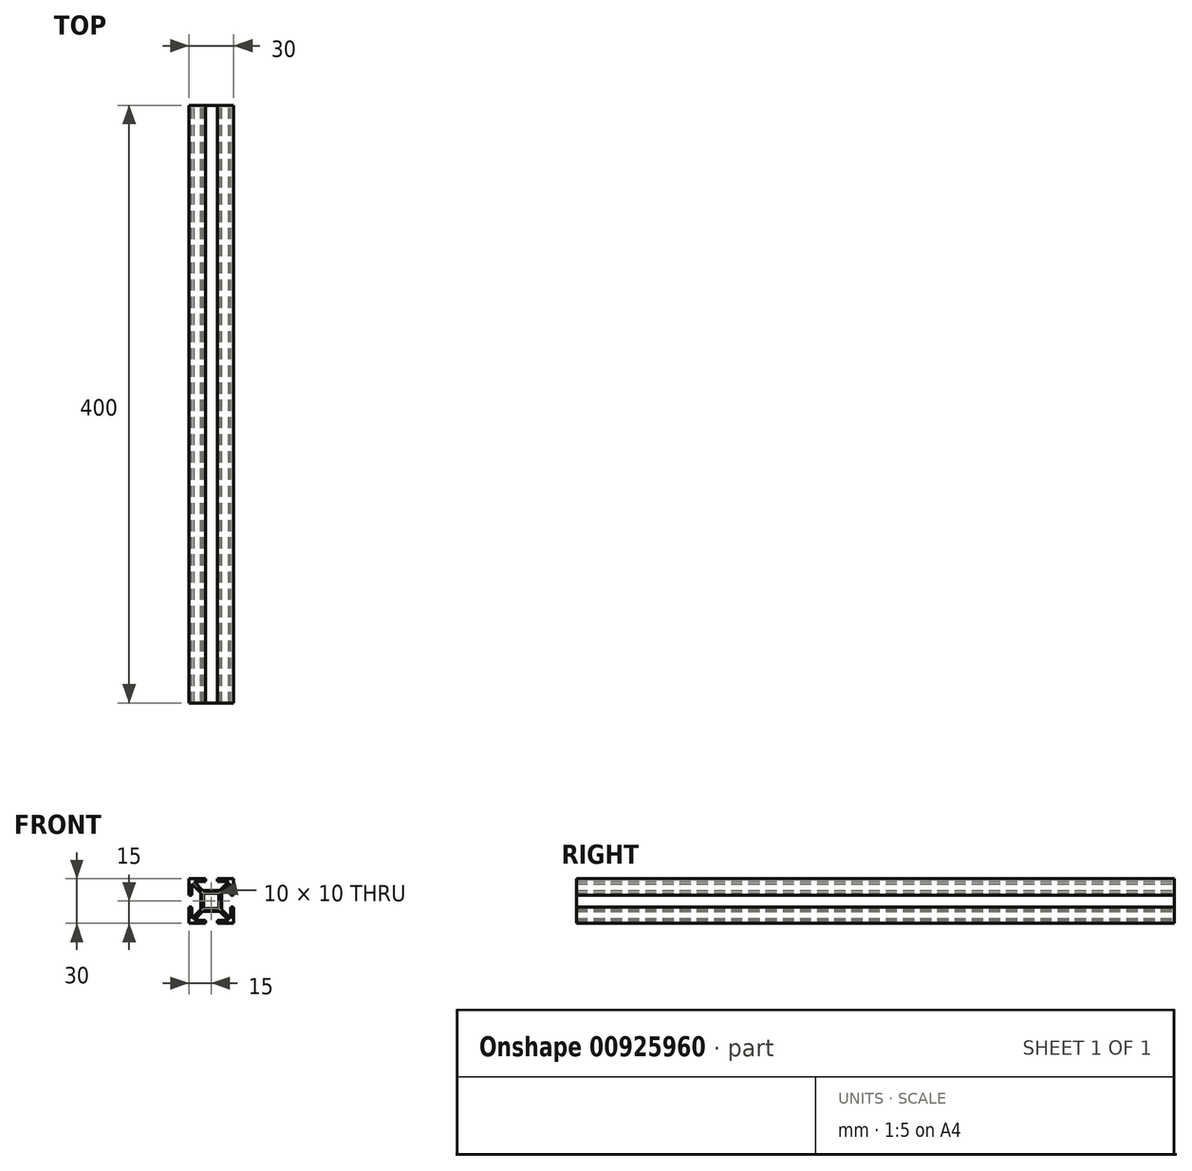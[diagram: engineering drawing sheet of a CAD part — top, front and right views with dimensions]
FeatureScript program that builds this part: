
annotation { "Feature Type Name" : "Feature", "Feature Type Description" : "" }
export const myFeature = defineFeature(function(context is Context, id is Id, definition is map)
    precondition{}
    {
        {
            var Q0;
            Q0=qCreatedBy(makeId("Front.planeOp"),FACE);
            var sketch = newSketch(context, id + "F0", { "sketchPlane" : qUnion([Q0])});
            skLineSegment(sketch, "E0.bottom", {"start": v(5, 5) * mm, "end": v(-5, 5) * mm});
            skLineSegment(sketch, "E0.top", {"start": v(5, -5) * mm, "end": v(-5, -5) * mm});
            skLineSegment(sketch, "E0.left", {"start": v(5, 5) * mm, "end": v(5, -5) * mm});
            skLineSegment(sketch, "E0.right", {"start": v(-5, 5) * mm, "end": v(-5, -5) * mm});
            skPoint(sketch, "E0.middle", {"position": v(0, 0) * mm});
            skLineSegment(sketch, "E1.0", {"start": v(7, -7) * mm, "end": v(-7, -7) * mm});
            skLineSegment(sketch, "E1.1", {"start": v(7, 7) * mm, "end": v(7, -7) * mm});
            skLineSegment(sketch, "E1.2", {"start": v(7, 7) * mm, "end": v(-7, 7) * mm});
            skLineSegment(sketch, "E1.3", {"start": v(-7, 7) * mm, "end": v(-7, -7) * mm});
            skLineSegment(sketch, "E2", {"start": v(-7, 7) * mm, "end": v(-13.08, 13.08) * mm, "construction": true});
            skLineSegment(sketch, "E3", {"start": v(-7, 5.59) * mm, "end": v(-13, 11.59) * mm});
            skLineSegment(sketch, "E4", {"start": v(-5.59, 7) * mm, "end": v(-11.59, 13) * mm});
            skLineSegment(sketch, "E5", {"start": v(-11.59, 13) * mm, "end": v(-4, 13) * mm});
            skLineSegment(sketch, "E6", {"start": v(-4, 13) * mm, "end": v(-4, 15) * mm});
            skLineSegment(sketch, "E7", {"start": v(-4, 15) * mm, "end": v(-15, 15) * mm});
            skLineSegment(sketch, "E8", {"start": v(-15, 15) * mm, "end": v(-15, 4) * mm});
            skLineSegment(sketch, "E9", {"start": v(-15, 4) * mm, "end": v(-13, 4) * mm});
            skLineSegment(sketch, "E10", {"start": v(-13, 4) * mm, "end": v(-13, 11.59) * mm});
            skLineSegment(sketch, "E11.1.0", {"start": v(-7, -7) * mm, "end": v(-13.08, -13.08) * mm, "construction": true});
            skLineSegment(sketch, "E11.1.1", {"start": v(-15, -4) * mm, "end": v(-15, -15) * mm});
            skLineSegment(sketch, "E11.1.2", {"start": v(-4, -13) * mm, "end": v(-11.59, -13) * mm});
            skLineSegment(sketch, "E11.1.3", {"start": v(-4, -15) * mm, "end": v(-4, -13) * mm});
            skLineSegment(sketch, "E11.1.4", {"start": v(-5.59, -7) * mm, "end": v(-11.59, -13) * mm});
            skLineSegment(sketch, "E11.1.5", {"start": v(-13, -4) * mm, "end": v(-15, -4) * mm});
            skLineSegment(sketch, "E11.1.6", {"start": v(-15, -15) * mm, "end": v(-4, -15) * mm});
            skLineSegment(sketch, "E11.1.7", {"start": v(-7, -5.59) * mm, "end": v(-13, -11.59) * mm});
            skLineSegment(sketch, "E11.1.8", {"start": v(-13, -11.59) * mm, "end": v(-13, -4) * mm});
            skLineSegment(sketch, "E11.2.0", {"start": v(7, -7) * mm, "end": v(13.08, -13.08) * mm, "construction": true});
            skLineSegment(sketch, "E11.2.1", {"start": v(4, -15) * mm, "end": v(15, -15) * mm});
            skLineSegment(sketch, "E11.2.2", {"start": v(13, -4) * mm, "end": v(13, -11.59) * mm});
            skLineSegment(sketch, "E11.2.3", {"start": v(15, -4) * mm, "end": v(13, -4) * mm});
            skLineSegment(sketch, "E11.2.4", {"start": v(7, -5.59) * mm, "end": v(13, -11.59) * mm});
            skLineSegment(sketch, "E11.2.5", {"start": v(4, -13) * mm, "end": v(4, -15) * mm});
            skLineSegment(sketch, "E11.2.6", {"start": v(15, -15) * mm, "end": v(15, -4) * mm});
            skLineSegment(sketch, "E11.2.7", {"start": v(5.59, -7) * mm, "end": v(11.59, -13) * mm});
            skLineSegment(sketch, "E11.2.8", {"start": v(11.59, -13) * mm, "end": v(4, -13) * mm});
            skLineSegment(sketch, "E11.3.0", {"start": v(7, 7) * mm, "end": v(13.08, 13.08) * mm, "construction": true});
            skLineSegment(sketch, "E11.3.1", {"start": v(15, 4) * mm, "end": v(15, 15) * mm});
            skLineSegment(sketch, "E11.3.2", {"start": v(4, 13) * mm, "end": v(11.59, 13) * mm});
            skLineSegment(sketch, "E11.3.3", {"start": v(4, 15) * mm, "end": v(4, 13) * mm});
            skLineSegment(sketch, "E11.3.4", {"start": v(5.59, 7) * mm, "end": v(11.59, 13) * mm});
            skLineSegment(sketch, "E11.3.5", {"start": v(13, 4) * mm, "end": v(15, 4) * mm});
            skLineSegment(sketch, "E11.3.6", {"start": v(15, 15) * mm, "end": v(4, 15) * mm});
            skLineSegment(sketch, "E11.3.7", {"start": v(7, 5.59) * mm, "end": v(13, 11.59) * mm});
            skLineSegment(sketch, "E11.3.8", {"start": v(13, 11.59) * mm, "end": v(13, 4) * mm});
            skSolve(sketch);
        }
        {
            var Q0;
            Q0 = qSketchRegion(id + "F0", true);
            extrude(context, id + "F1", {"entities" : qUnion([Q0]), "endBound" : BoundingType.SYMMETRIC, "depth" : 400 * mm, "offsetDistance" : 25 * mm});
        }
    });
